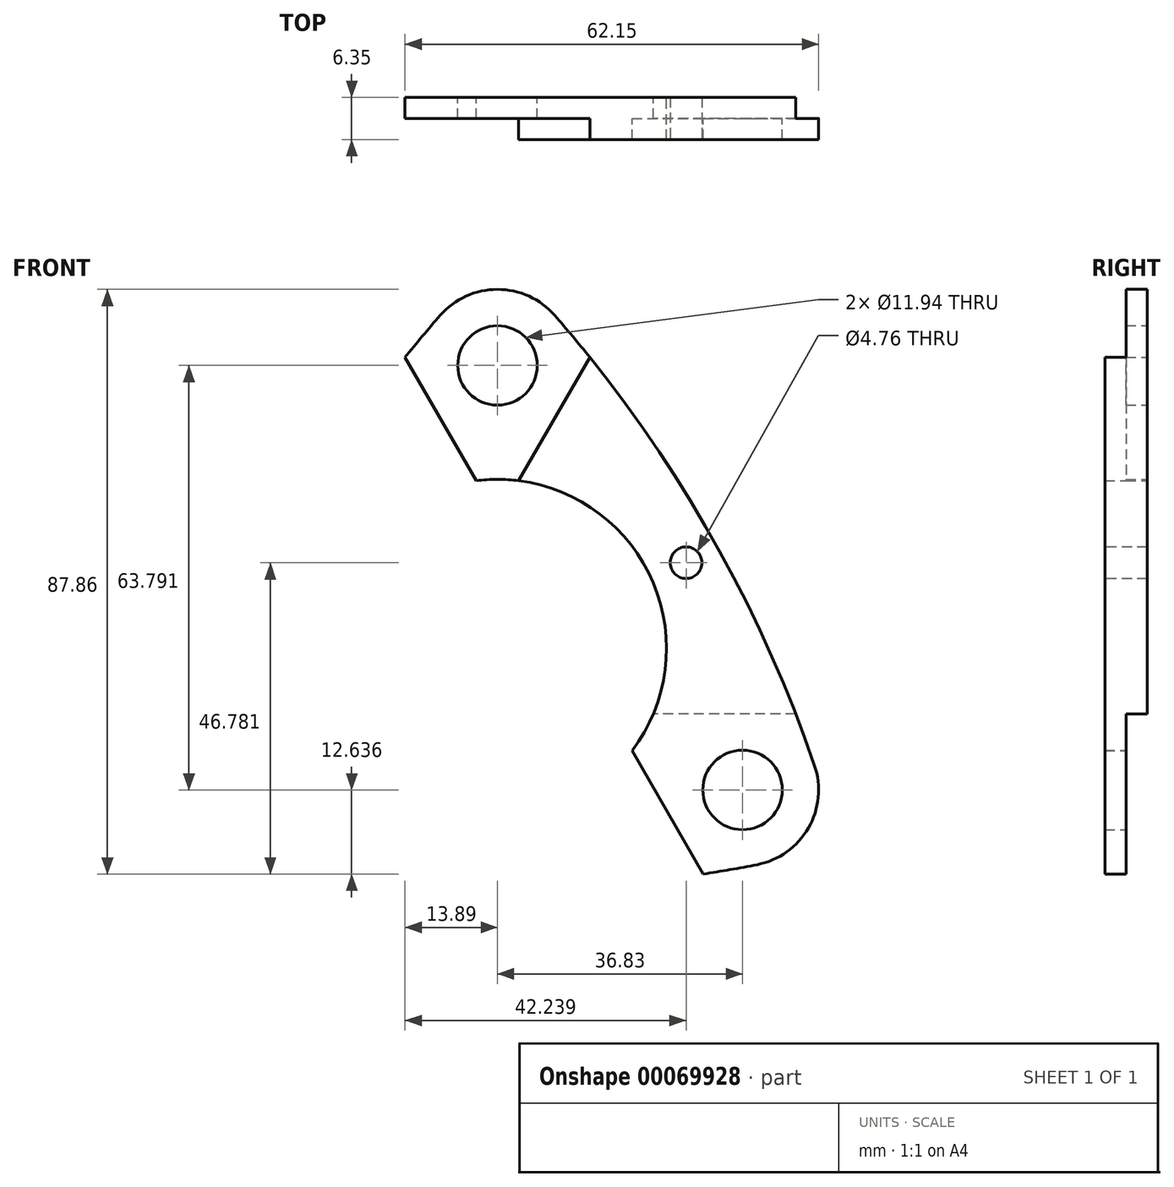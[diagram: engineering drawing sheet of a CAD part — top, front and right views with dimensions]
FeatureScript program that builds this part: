
annotation { "Feature Type Name" : "Feature", "Feature Type Description" : "" }
export const myFeature = defineFeature(function(context is Context, id is Id, definition is map)
    precondition{}
    {
        {
            var Q0;
            Q0=qCreatedBy(makeId("Front.planeOp"),FACE);
            var sketch = newSketch(context, id + "F0", { "sketchPlane" : qUnion([Q0])});
            skArc(sketch, "E0", {"start": v(20.23, -15.36) * mm, "mid": v(22, 12.7) * mm, "end": v(-3.2, 25.2) * mm});
            skLineSegment(sketch, "E1", {"start": v(0, 59.33) * mm, "end": v(0, -96.32) * mm, "construction": true});
            skLineSegment(sketch, "E2", {"start": v(-68.49, 39.54) * mm, "end": v(97.23, -56.14) * mm, "construction": true});
            skLineSegment(sketch, "E3", {"start": v(91.73, 52.96) * mm, "end": v(-72.7, -41.98) * mm, "construction": true});
            skCircle(sketch, "E4", {"center": v(0, 0) * mm, "radius": 42.53 * mm, "construction": true});
            skCircle(sketch, "E5", {"center": v(0, 42.53) * mm, "radius": 11.43 * mm, "construction": true});
            skCircle(sketch, "E6", {"center": v(36.83, -21.26) * mm, "radius": 11.43 * mm, "construction": true});
            skCircle(sketch, "E7", {"center": v(-36.83, -21.26) * mm, "radius": 11.43 * mm, "construction": true});
            skCircle(sketch, "E8", {"center": v(0, 42.53) * mm, "radius": 5.97 * mm});
            skCircle(sketch, "E9", {"center": v(36.83, -21.26) * mm, "radius": 5.97 * mm});
            skArc(sketch, "E10", {"start": v(47.64, -17.56) * mm, "mid": v(31.4, 18.13) * mm, "end": v(8.62, 50.04) * mm});
            skArc(sketch, "E11", {"start": v(30.93, -33.9) * mm, "mid": v(34.98, -33.23) * mm, "end": v(39.03, -32.48) * mm});
            skArc(sketch, "E12", {"start": v(-8.62, 50.04) * mm, "mid": v(-11.29, 46.91) * mm, "end": v(-13.9, 43.73) * mm});
            skArc(sketch, "E13.filletArc", {"start": v(39.03, -32.48) * mm, "mid": v(46.73, -26.98) * mm, "end": v(47.64, -17.56) * mm});
            skArc(sketch, "E14.filletArc", {"start": v(8.62, 50.04) * mm, "mid": v(0, 53.96) * mm, "end": v(-8.62, 50.04) * mm});
            skLineSegment(sketch, "E15", {"start": v(-13.9, 43.73) * mm, "end": v(-3.2, 25.2) * mm});
            skPoint(sketch, "E16.orphan", {"position": v(-115.86, 0) * mm});
            skLineSegment(sketch, "E17.trimOffspring", {"start": v(20.23, -15.36) * mm, "end": v(30.93, -33.9) * mm});
            skSolve(sketch);
        }
        {
            var Q0;
            Q0=makeQuery(id+"F0.imprint","IMPRINT",FACE,{"disambiguationData":[TD([[makeQuery(id+"F0.imprint","IMPRINT",EDGE,{"derivedFrom":sQuery(id+"F0.wireOp",EDGE,"E0")}),-1.0]])]});
            extrude(context, id + "F1", {"entities" : qUnion([Q0]), "depth" : 6.35 * mm});
        }
        {
            var Q0;
            Q0=makeQuery(id+"F1.opExtrude","CAP_FACE",FACE,{"disambiguationData":[OSD([sQuery(id+"F0.wireOp",EDGE,"E0"),sQuery(id+"F0.wireOp",EDGE,"E8"),sQuery(id+"F0.wireOp",EDGE,"E9"),sQuery(id+"F0.wireOp",EDGE,"E10"),sQuery(id+"F0.wireOp",EDGE,"E11"),sQuery(id+"F0.wireOp",EDGE,"E12"),sQuery(id+"F0.wireOp",EDGE,"E13.filletArc"),sQuery(id+"F0.wireOp",EDGE,"E14.filletArc"),sQuery(id+"F0.wireOp",EDGE,"E15"),sQuery(id+"F0.wireOp",EDGE,"E17.trimOffspring")])],"isStart":false});
            var sketch = newSketch(context, id + "F2", { "sketchPlane" : qUnion([Q0])});
            skLineSegment(sketch, "E18", {"start": v(-6.94, 7.64) * mm, "end": v(20.57, 55.3) * mm});
            skLineSegment(sketch, "E19", {"start": v(20.57, 55.3) * mm, "end": v(-11.7, 73.93) * mm});
            skLineSegment(sketch, "E20", {"start": v(-11.7, 73.93) * mm, "end": v(-39.2, 26.27) * mm});
            skLineSegment(sketch, "E21", {"start": v(-39.2, 26.27) * mm, "end": v(-6.94, 7.64) * mm});
            skSolve(sketch);
        }
        {
            var Q0;
            Q0 = qSketchRegion(id + "F2", true);
            extrude(context, id + "F3", {"entities" : qUnion([Q0]), "operationType" : NewBodyOperationType.REMOVE, "oppositeDirection" : true, "depth" : 3.17 * mm});
        }
        {
            var Q0;
            Q0=makeQuery(id+"F0.imprint","IMPRINT",FACE,{"disambiguationData":[TD([[makeQuery(id+"F0.imprint","IMPRINT",EDGE,{"derivedFrom":sQuery(id+"F0.wireOp",EDGE,"E0")}),-1.0]])]});
            var sketch = newSketch(context, id + "F4", { "sketchPlane" : qUnion([Q0])});
            skLineSegment(sketch, "E22", {"start": v(65.58, -9.83) * mm, "end": v(1.77, -9.83) * mm});
            skLineSegment(sketch, "E23", {"start": v(1.77, -9.83) * mm, "end": v(1.77, -59.23) * mm});
            skLineSegment(sketch, "E24", {"start": v(1.77, -59.23) * mm, "end": v(65.58, -59.23) * mm});
            skLineSegment(sketch, "E25", {"start": v(65.58, -59.23) * mm, "end": v(65.58, -9.83) * mm});
            skSolve(sketch);
        }
        {
            var Q0;
            Q0=makeQuery(id+"F4.imprint","IMPRINT",FACE,{"disambiguationData":[TD([[makeQuery(id+"F4.imprint","IMPRINT",EDGE,{"derivedFrom":makeQuery(id+"F0.imprint","IMPRINT",EDGE,{"derivedFrom":sQuery(id+"F0.wireOp",EDGE,"E9")})}),1.0]])]});
            var Q1;
            {var subQ0=sQuery(id+"F4.wireOp",EDGE,"E23");Q1=makeQuery(id+"F4.imprint","IMPRINT",FACE,{"disambiguationData":[TD([[makeQuery(id+"F4.imprint","IMPRINT",EDGE,{"derivedFrom":subQ0}),1.0]])]});}
            var Q2;
            Q2=makeQuery(id+"F4.imprint","IMPRINT",FACE,{"disambiguationData":[TD([[makeQuery(id+"F4.imprint","IMPRINT",EDGE,{"derivedFrom":makeQuery(id+"F0.imprint","IMPRINT",EDGE,{"derivedFrom":sQuery(id+"F0.wireOp",EDGE,"E9")})}),-1.0]])]});
            extrude(context, id + "F5", {"entities" : qUnion([Q0, Q1, Q2]), "operationType" : NewBodyOperationType.REMOVE, "depth" : 3.17 * mm});
        }
        {
            var Q0;
            Q0=makeQuery(id+"F1.opExtrude","CAP_FACE",FACE,{"disambiguationData":[OSD([sQuery(id+"F0.wireOp",EDGE,"E0"),sQuery(id+"F0.wireOp",EDGE,"E8"),sQuery(id+"F0.wireOp",EDGE,"E9"),sQuery(id+"F0.wireOp",EDGE,"E10"),sQuery(id+"F0.wireOp",EDGE,"E11"),sQuery(id+"F0.wireOp",EDGE,"E12"),sQuery(id+"F0.wireOp",EDGE,"E13.filletArc"),sQuery(id+"F0.wireOp",EDGE,"E14.filletArc"),sQuery(id+"F0.wireOp",EDGE,"E15"),sQuery(id+"F0.wireOp",EDGE,"E17.trimOffspring")])],"isStart":false});
            var sketch = newSketch(context, id + "F6", { "sketchPlane" : qUnion([Q0])});
            skCircle(sketch, "E26", {"center": v(28.35, 12.88) * mm, "radius": 2.38 * mm});
            skSolve(sketch);
        }
        {
            var Q0;
            Q0 = qSketchRegion(id + "F6", true);
            extrude(context, id + "F7", {"entities" : qUnion([Q0]), "operationType" : NewBodyOperationType.REMOVE, "oppositeDirection" : true, "depth" : 25.4 * mm});
        }
    });
